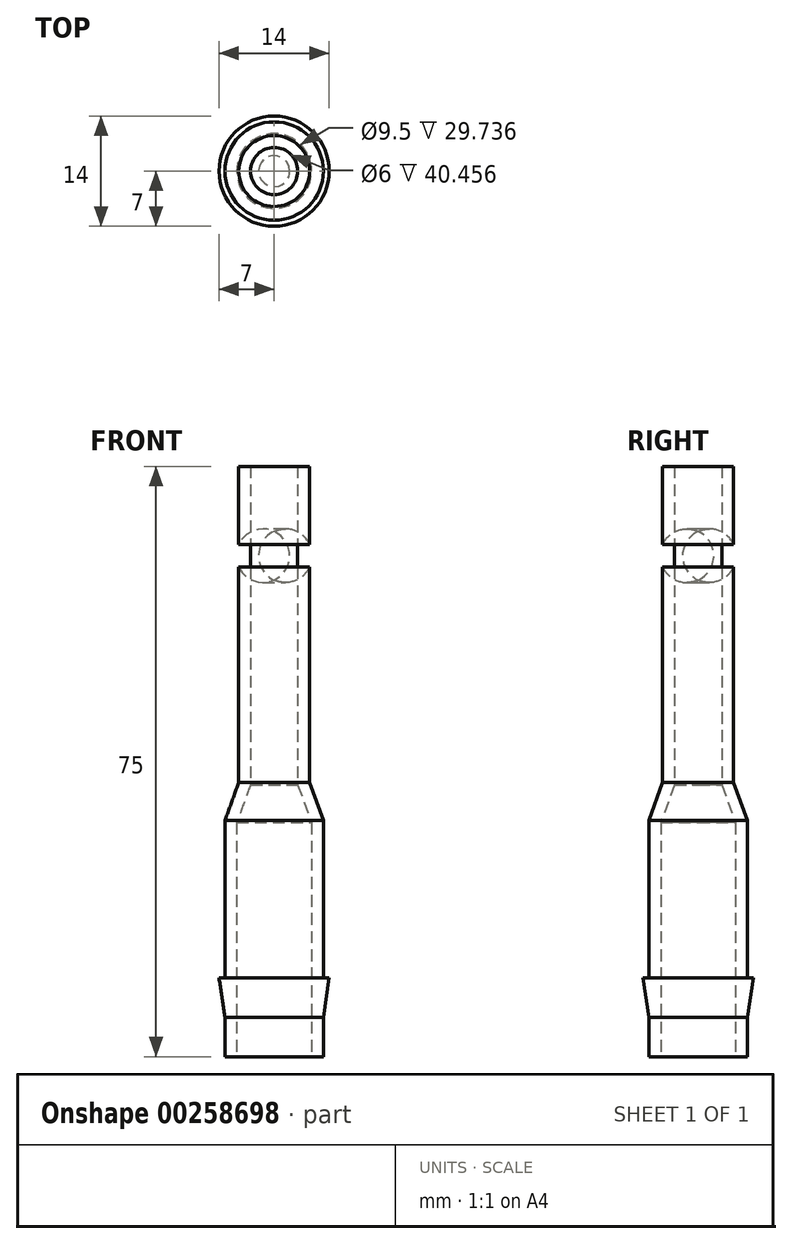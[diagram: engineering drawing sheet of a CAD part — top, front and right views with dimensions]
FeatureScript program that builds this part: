
annotation { "Feature Type Name" : "Feature", "Feature Type Description" : "" }
export const myFeature = defineFeature(function(context is Context, id is Id, definition is map)
    precondition{}
    {
        {
            var Q0;
            Q0=qCreatedBy(makeId("Front.planeOp"),FACE);
            var sketch = newSketch(context, id + "F0", { "sketchPlane" : qUnion([Q0])});
            skLineSegment(sketch, "E0", {"start": v(6.25, 0) * mm, "end": v(6.25, 5) * mm});
            skLineSegment(sketch, "E1", {"start": v(6.25, 5) * mm, "end": v(7, 10) * mm});
            skLineSegment(sketch, "E2", {"start": v(7, 10) * mm, "end": v(6.25, 10) * mm});
            skLineSegment(sketch, "E3", {"start": v(6.25, 10) * mm, "end": v(6.25, 30) * mm});
            skLineSegment(sketch, "E4", {"start": v(4.75, 0) * mm, "end": v(4.75, 29.74) * mm});
            skLineSegment(sketch, "E5", {"start": v(4.75, 29.74) * mm, "end": v(3, 34.54) * mm});
            skLineSegment(sketch, "E6", {"start": v(6.25, 30) * mm, "end": v(4.5, 34.8) * mm});
            skLineSegment(sketch, "E7", {"start": v(4.5, 34.8) * mm, "end": v(4.5, 75) * mm});
            skLineSegment(sketch, "E8", {"start": v(4.5, 75) * mm, "end": v(3, 75) * mm});
            skLineSegment(sketch, "E9", {"start": v(3, 75) * mm, "end": v(3, 34.54) * mm});
            skLineSegment(sketch, "E10", {"start": v(0, 0) * mm, "end": v(0, 71.56) * mm, "construction": true});
            skLineSegment(sketch, "E11", {"start": v(6.25, 0) * mm, "end": v(4.75, 0) * mm});
            skSolve(sketch);
        }
        {
            var Q0;
            Q0 = qSketchRegion(id + "F0", true);
            var Q1;
            Q1=sQuery(id+"F0.wireOp",EDGE,"E10");
            revolve(context, id + "F1", {"entities" : qUnion([Q0]), "axis" : qUnion([Q1]), "revolveType" : RevolveType.FULL});
        }
        {
            var Q0;
            Q0=qCreatedBy(makeId("Right.planeOp"),FACE);
            var sketch = newSketch(context, id + "F2", { "sketchPlane" : qUnion([Q0])});
            skArc(sketch, "E12", {"start": v(4.4, 61.99) * mm, "mid": v(4.83, 63.64) * mm, "end": v(4.4, 65.29) * mm});
            skLineSegment(sketch, "E13", {"start": v(4.4, 61.99) * mm, "end": v(4.4, 65.29) * mm});
            skPoint(sketch, "E14", {"position": v(4.83, 63.64) * mm});
            skLineSegment(sketch, "E15", {"start": v(0, 51.13) * mm, "end": v(0, 70.57) * mm, "construction": true});
            skSolve(sketch);
        }
        {
            var Q0;
            Q0 = qSketchRegion(id + "F2", true);
            var Q1;
            Q1=sQuery(id+"F2.wireOp",EDGE,"E15");
            revolve(context, id + "F3", {"operationType" : NewBodyOperationType.ADD, "entities" : qUnion([Q0]), "axis" : qUnion([Q1]), "revolveType" : RevolveType.FULL});
        }
    });
